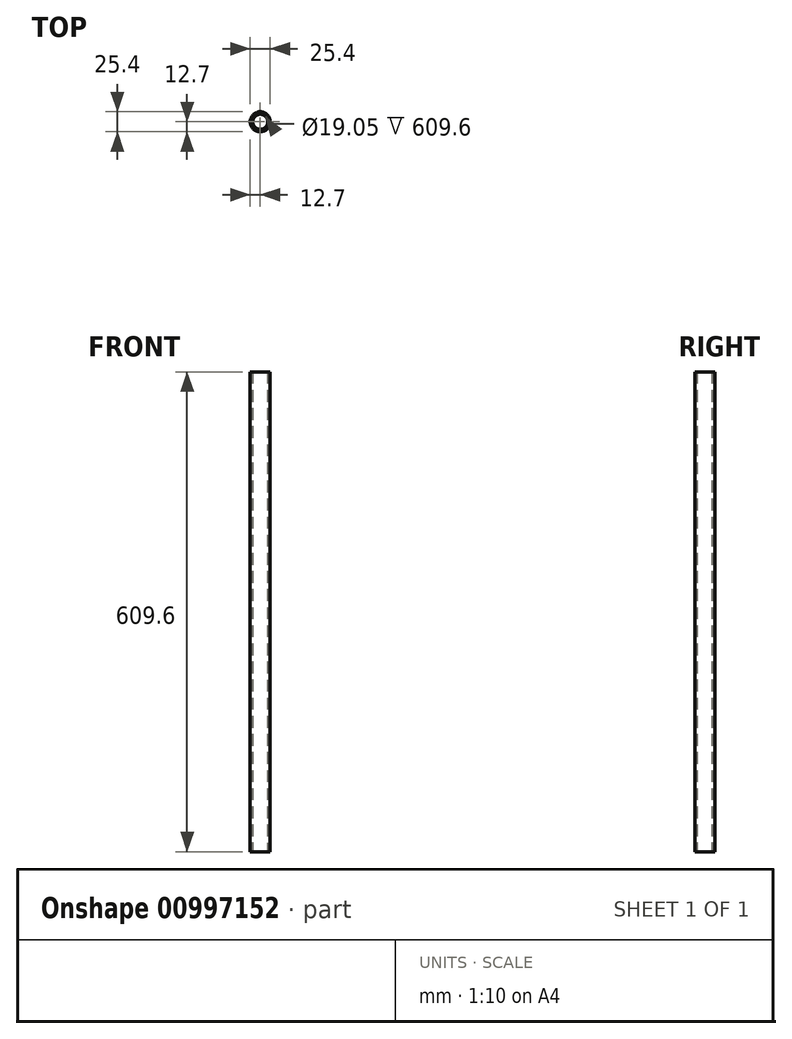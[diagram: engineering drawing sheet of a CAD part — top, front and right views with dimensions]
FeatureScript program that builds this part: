
annotation { "Feature Type Name" : "Feature", "Feature Type Description" : "" }
export const myFeature = defineFeature(function(context is Context, id is Id, definition is map)
    precondition{}
    {
        {
            var Q0;
            Q0=qCreatedBy(makeId("Top.planeOp"),FACE);
            var sketch = newSketch(context, id + "F0", { "sketchPlane" : qUnion([Q0])});
            skCircle(sketch, "E0", {"center": v(0, 0) * mm, "radius": 12.7 * mm});
            skCircle(sketch, "E1.0", {"center": v(0, 0) * mm, "radius": 9.53 * mm});
            skSolve(sketch);
        }
        {
            var Q0;
            Q0 = qSketchRegion(id + "F0", true);
            extrude(context, id + "F1", {"entities" : qUnion([Q0]), "depth" : 609.6 * mm, "offsetDistance" : 25.4 * mm, "symmetric" : true});
        }
    });
